# Revit family: FalsoTecho_THU_Bandeja-Siena
name_source: partatom
category: Modelos genéricos
revit_build: Autodesk Revit 2016 (Build: 20160720_0715(x64)
units: mm (PartAtom-declared; Revit-internal decimal feet)

## family parameters
Compartido = Sí
Corte con vacíos al cargar = Sí
Cota de conector redondo = Diámetro de uso
Puede alojar armadura = No
Punto de cálculo de habitación = No
Se basa en plano de trabajo = Sí
Siempre vertical = No
Tipo de pieza = Normal

## types (2) — shared parameters
Bandeja_Espesor = 1 mm  [stored 0.00328084 ft]
Bandeja_Grosor = 35 mm  [stored 0.114829 ft]
Bandeja_Longitud = 340 mm  [stored 1.11549 ft]
COBie Type Category = L387 : Suspended ceilings
Comentarios de tipo = Bandeja Siena para techo suspendido, para ser montados en interior de edificios con perfilería THU T24 o perfilería DP.
Descripción = Bandeja THU de 300 x 1200 mm. de longitud de cantos biselados preparada para su instalación sobre perfiles primarios desmontables sean T24, T15 , T35 o perfiles anchos DP en sus diversas medidas. Fabricadas en acero galvanizado o en aluminio, las placas una vez instaladas quedan atestadas las unas unas contra las otras en sus lados longitudinales largos de 1200 mm., y apoyadas descolgadas respecto del perfil en sus lados lados cortos 8 mm., lo que le confiere un rápido y fácil registro en cualquier punto.
Fabricante = THU Perfil S.L.
Famila del producto = Techos metálicos
Grupo del producto = Bandejas
IFC Classification = IfcCovering (CEILING)
Marca = THU
NBS Reference = 20-10-10/110
NBS Reference Description = Board suspended ceiling system
Nombre del objeto = Bandeja Siena 300x1200
Omniclass = 23-15 19 23 11
Perfil T15 Primario = Perfil_THU_T15 : Perfil T15-Primario
Perfil T24 Primario = Perfil_THU_T24 : Perfil T24-Primario
Perfil perimetral_Desfase vertical = 1 mm  [stored 0.00328084 ft]
Página web del fabricante = http://thu.es
Solape_Perfil y tirante = 7 mm  [stored 0.0229659 ft]
THU_Bandeja = Bandeja_THU_Siena-300x1200 : 300x1200
THU_Reacción al fuego = A2, s1-d0
THU_Subestructura_Material = Acero galvanizado
zero-valued in all types: Bandejas_Separación long, Elevación por defecto, Número de edición (versión)

## per-type parameters (varying)
| type | Perfil DP100 | THU_Bandeja_Material |
| Acero_300x1200 | Perfil_THU_DP(100) : Perfil DP100-Primario | Acero |
| Aluminio_300x1200 | Bandeja_THU_Siena-300x1200 : 300x1200 | Aluminio |

note: [stored X ft] marks values corroborated as IEEE doubles in the binary element streams (Revit-internal decimal feet)
